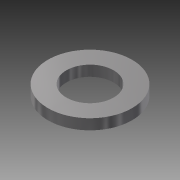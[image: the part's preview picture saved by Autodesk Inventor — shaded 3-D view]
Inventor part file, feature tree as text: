
AUTODESK INVENTOR PART (.ipt)
format: ipt  version: 2013 (Build 170138000, 138)  size: 79,360 bytes
history: native  units: mm
features: other x1, extrude x1, sketch x1
ambient origin geometry x1: Origin
feature tree (3):
  other  "ソリッド1"
  extrude  "押し出し1"  Depth=4.5mm
  sketch  "スケッチ1"
